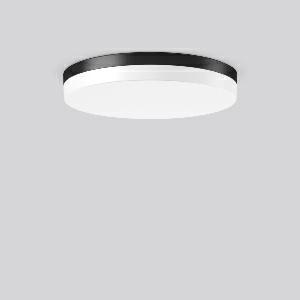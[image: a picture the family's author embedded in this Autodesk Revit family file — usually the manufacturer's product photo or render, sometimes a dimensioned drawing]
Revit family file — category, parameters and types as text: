
# Revit family: flat_slim_round_312634_0031_19_1d4b
name_source: partatom
category: Lighting Fixtures
units: mm (PartAtom-declared; Revit-internal decimal feet)

## family parameters
Cut with Voids When Loaded = No
Host = Face
Light Source = No
Part Type = Normal
Room Calculation Point = No
Round Connector Dimension = Use Diameter
Shared = No

## types (1)
- MultiLumen 1 830 (1 x LED Modul 830, 3450 lm, 3000)
    Apparent Load = 26 VA
    CIE Flux Codes = 40 71 90 84 100
    Color Rendering = 80
    Color Temperature = 3000
    Default Elevation = 1800 mm
    Height = 70 mm
    Lamp = 1 x LED Modul 830
    Lamp Light Flux = 3450 lm
    Lamp count = 1
    Length = 480 mm
    Lifetime = 50000 h
    Luminous efficacy = 133 lm/W
    Manufacturer = RZB
    ModVariant = No
    Model = 312634.0031.19
    Mounting Place = Ceiling
    Mounting Type = Surface mounted
    Number of Poles = 1
    OnlyDefault = Yes
    Power Factor = 1
    Product Name = FLAT SLIM round
    Product group = Surface mounted ceiling and wall luminaires
    ProductGroupID = 305
    Protection Class = Protection class I
    Protection Degree = Degree of protection
    RLX_Detail_Level = 1
    RLX_Emergency_Light_Flux = 0 lm
    RLX_Emergency_Type = 0
    RLX_Emergency_Type_DB = No
    RlxData = <blob elided: 23513 chars, md5=a142cdb5>
    Socket = socket
    Standby Power = 0 W
    System Light Flux = 3450 lm
    System Power = 26 W
    Type Comments = MultiLumen 1 830
    Type Image = 312633.0031.jpg
    URL = http://relux.com
    VarID = multilumen_1_830
    Voltage = 0 V
    Weight = 0.00 kg
    Width = 0 mm  [stored 0 ft]

note: [stored X ft] marks values corroborated as IEEE doubles in the binary element streams (Revit-internal decimal feet)

## geometry (parser evidence)
native form markers: Blend x4, Sweep x12
no freeform markers — native parametric forms only
